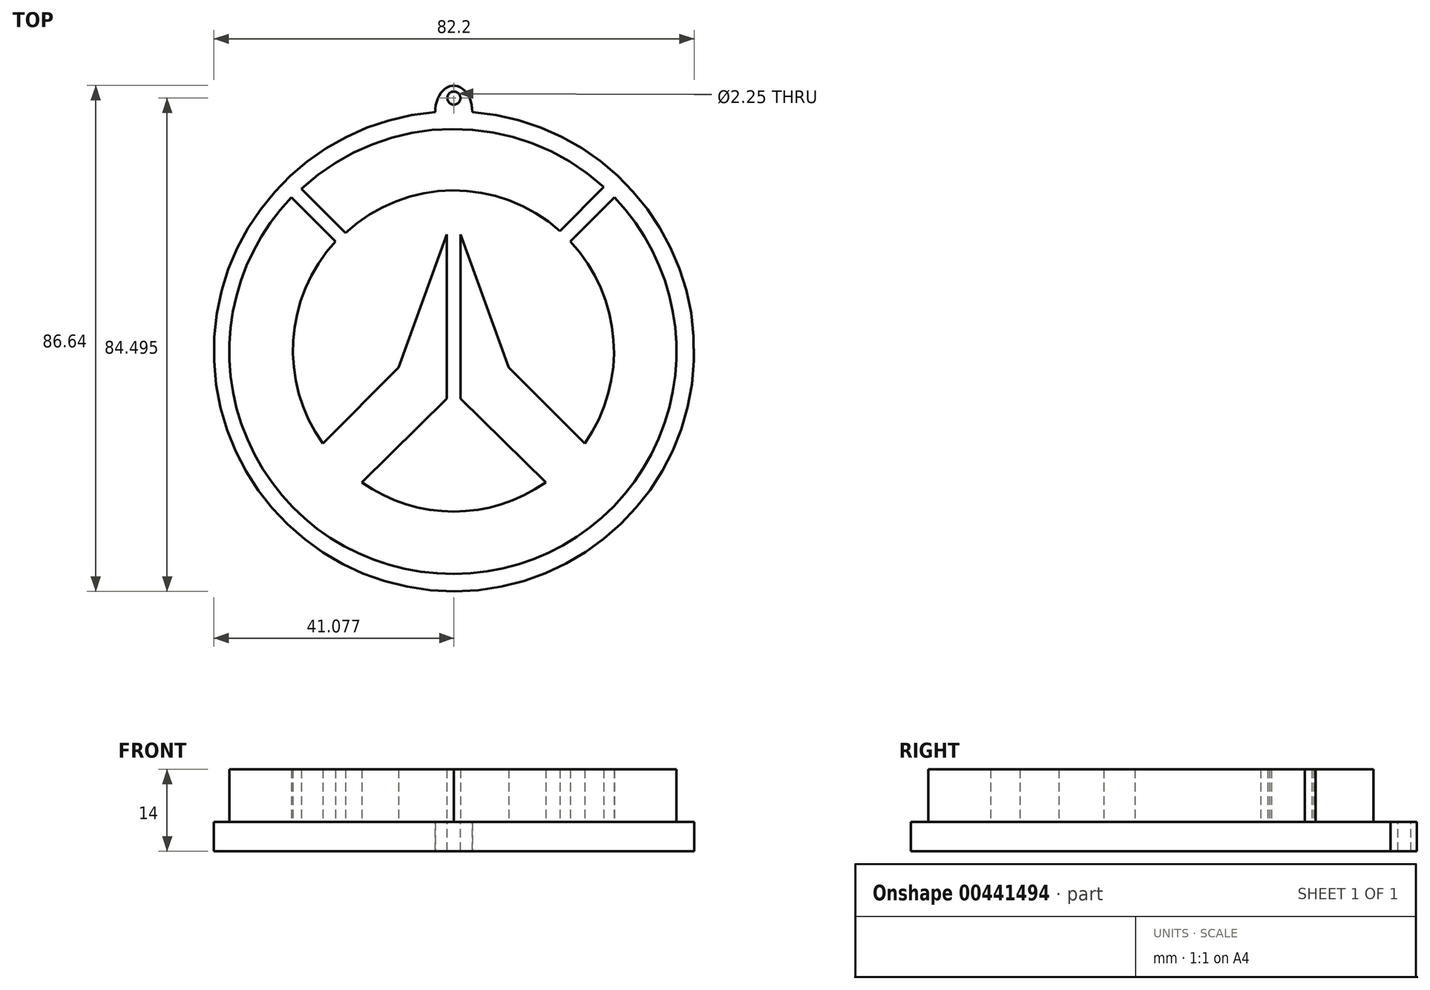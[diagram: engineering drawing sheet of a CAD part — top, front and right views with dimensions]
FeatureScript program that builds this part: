
annotation { "Feature Type Name" : "Feature", "Feature Type Description" : "" }
export const myFeature = defineFeature(function(context is Context, id is Id, definition is map)
    precondition{}
    {
        {
            var Q0;
            Q0=qCreatedBy(makeId("Top.planeOp"),FACE);
            var sketch = newSketch(context, id + "F0", { "sketchPlane" : qUnion([Q0])});
            skArc(sketch, "E0", {"start": v(25.67, 27.45) * mm, "mid": v(-0.26, 37.38) * mm, "end": v(-26.07, 27.13) * mm});
            skLineSegment(sketch, "E1", {"start": v(25.67, 27.45) * mm, "end": v(18.2, 19.89) * mm});
            skLineSegment(sketch, "E2", {"start": v(-26.07, 27.13) * mm, "end": v(-18.51, 19.6) * mm});
            skArc(sketch, "E3", {"start": v(18.2, 19.89) * mm, "mid": v(-0.21, 26.85) * mm, "end": v(-18.51, 19.6) * mm});
            skArc(sketch, "E4", {"start": v(0, -38.82) * mm, "mid": v(35.07, -15.68) * mm, "end": v(27.5, 25.65) * mm});
            skArc(sketch, "E5", {"start": v(-27.79, 25.65) * mm, "mid": v(-35.33, -15.82) * mm, "end": v(0, -38.82) * mm});
            skArc(sketch, "E6", {"start": v(-20.26, 18.09) * mm, "mid": v(-27.49, 1.17) * mm, "end": v(-22.42, -16.5) * mm});
            skArc(sketch, "E7", {"start": v(-15.74, -23.16) * mm, "mid": v(0, -28.16) * mm, "end": v(15.74, -23.16) * mm});
            skArc(sketch, "E8", {"start": v(22.41, -16.5) * mm, "mid": v(27.34, 1.23) * mm, "end": v(19.97, 18.09) * mm});
            skLineSegment(sketch, "E9", {"start": v(-27.79, 25.65) * mm, "end": v(-20.26, 18.09) * mm});
            skLineSegment(sketch, "E10", {"start": v(-22.42, -16.5) * mm, "end": v(-9.44, -3.48) * mm});
            skLineSegment(sketch, "E11", {"start": v(-9.44, -3.48) * mm, "end": v(-1.17, 19.3) * mm});
            skLineSegment(sketch, "E12", {"start": v(-1.17, 19.3) * mm, "end": v(-1.17, -8.82) * mm});
            skLineSegment(sketch, "E13", {"start": v(-15.74, -23.16) * mm, "end": v(-1.17, -8.82) * mm});
            skLineSegment(sketch, "E14", {"start": v(1.16, -8.82) * mm, "end": v(15.74, -23.16) * mm});
            skLineSegment(sketch, "E15", {"start": v(1.16, -8.82) * mm, "end": v(1.16, 19.3) * mm});
            skLineSegment(sketch, "E16", {"start": v(1.16, 19.3) * mm, "end": v(9.43, -3.48) * mm});
            skLineSegment(sketch, "E17", {"start": v(9.43, -3.48) * mm, "end": v(22.41, -16.5) * mm});
            skLineSegment(sketch, "E18", {"start": v(19.97, 18.09) * mm, "end": v(27.5, 25.65) * mm});
            skSolve(sketch);
        }
        {
            var Q0;
            Q0=makeQuery(id+"F0.imprint","IMPRINT",FACE,{"disambiguationData":[TD([[makeQuery(id+"F0.imprint","IMPRINT",EDGE,{"derivedFrom":sQuery(id+"F0.wireOp",EDGE,"E4")}),1.0]])]});
            var Q1;
            Q1=makeQuery(id+"F0.imprint","IMPRINT",FACE,{"disambiguationData":[TD([[makeQuery(id+"F0.imprint","IMPRINT",EDGE,{"derivedFrom":sQuery(id+"F0.wireOp",EDGE,"E0")}),1.0]])]});
            extrude(context, id + "F1", {"entities" : qUnion([Q0, Q1]), "depth" : 9 * mm});
        }
        {
            var Q0;
            Q0=qCreatedBy(makeId("Top.planeOp"),FACE);
            var sketch = newSketch(context, id + "F2", { "sketchPlane" : qUnion([Q0])});
            skCircle(sketch, "E19", {"center": v(0.04, -0.72) * mm, "radius": 41.1 * mm});
            skEllipse(sketch, "E20", {"center": v(0, 40.38) * mm, "majorRadius": 4.44 * mm, "minorRadius": 3.16 * mm, "majorAxis": v(0, -1)});
            skCircle(sketch, "E21", {"center": v(0.02, 42.67) * mm, "radius": 1.13 * mm});
            skSolve(sketch);
        }
        {
            var Q0;
            Q0 = qSketchRegion(id + "F2", true);
            extrude(context, id + "F3", {"entities" : qUnion([Q0]), "oppositeDirection" : true, "depth" : 5 * mm});
        }
    });
